# Revit family: TYCO-FPP-Zettler-SNM800 sounder notification module
name_source: partatom
category: Electrical Fixtures
revit_build: Autodesk Revit 2014 (Build: 20130308_1515(x64)
units: mm (PartAtom-declared; Revit-internal decimal feet)

## types (1)
- TYCO-FPP-Zettler-SNM800 sounder notification module
    Ambient Temperature = –25°C to +70°C
    Description = The SNM800 is a remote addressable sounder circuit
output device capable of switching sounder and speaker
circuits up to 2A @ 24V d.c.
    External Supply = 18 to 28.7Vdc
    Front Cover = Yes
    Keynote = Addressable switched output with supervised
output wiring
    Length = 61 mm
    Loop Voltage = 20V to 40Vdc
    Manufacturer = Tyco
    Max. SNM800 per Loop = 200/250
    Model = Zettler-577.800.005
    Operated Current = 3mA
    Output Current = 2A
    Output Current EOL = 27k Ohm 0.5W
    PCB = PCB
    Quiescent Current = 450μA
    RS = RS
    RS1 = RS(11)
    Rear Cover = Yes
    Relative Humidity = 10% to 95%
    ST = STT
    Storage Temperature = –40°C to +80°C
    Type Comments = The SNM800 can be
configured with a RIM800 to provide a secure monitored
extinguishing release solenoid control.
    URL = https://www.tycosafetyproducts-anz.com
    Width = 84 mm
    Wire Size (maximum) = 2.5sq. mm
    rs2 = RS(2)

## geometry (parser evidence)
native form markers: Sweep x6
no freeform markers — native parametric forms only
